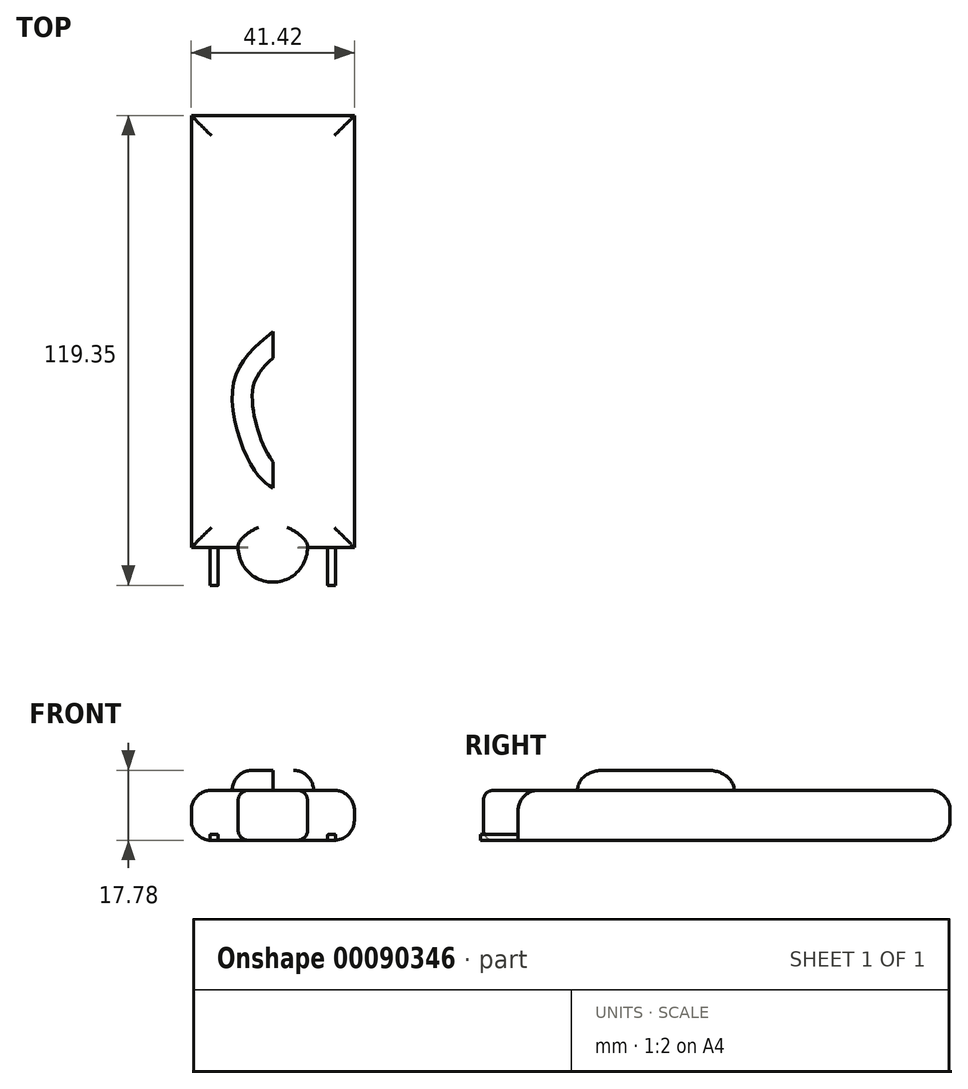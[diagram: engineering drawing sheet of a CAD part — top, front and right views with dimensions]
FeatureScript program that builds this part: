
annotation { "Feature Type Name" : "Feature", "Feature Type Description" : "" }
export const myFeature = defineFeature(function(context is Context, id is Id, definition is map)
    precondition{}
    {
        {
            var Q0;
            Q0=qCreatedBy(makeId("Top.planeOp"),FACE);
            var sketch = newSketch(context, id + "F0", { "sketchPlane" : qUnion([Q0])});
            skLineSegment(sketch, "E0.bottom", {"start": v(20.7, 54.87) * mm, "end": v(-20.7, 54.87) * mm});
            skLineSegment(sketch, "E0.top", {"start": v(20.7, -54.87) * mm, "end": v(-20.7, -54.87) * mm});
            skLineSegment(sketch, "E0.left", {"start": v(20.7, 54.87) * mm, "end": v(20.7, -54.87) * mm});
            skLineSegment(sketch, "E0.right", {"start": v(-20.7, 54.87) * mm, "end": v(-20.7, -54.87) * mm});
            skPoint(sketch, "E0.middle", {"position": v(0, 0) * mm});
            skLineSegment(sketch, "E1.bottom", {"start": v(15.97, -64.48) * mm, "end": v(13.9, -64.48) * mm});
            skLineSegment(sketch, "E1.top", {"start": v(15.97, -45.26) * mm, "end": v(13.9, -45.26) * mm});
            skLineSegment(sketch, "E1.left", {"start": v(15.97, -64.48) * mm, "end": v(15.97, -45.26) * mm});
            skLineSegment(sketch, "E1.right", {"start": v(13.9, -64.48) * mm, "end": v(13.9, -45.26) * mm});
            skPoint(sketch, "E1.middle", {"position": v(14.94, -54.87) * mm});
            skCircle(sketch, "E2", {"center": v(0, -54.87) * mm, "radius": 8.8 * mm});
            skLineSegment(sketch, "E3", {"start": v(0, 62.86) * mm, "end": v(0, -73.65) * mm});
            skLineSegment(sketch, "E4.MirrorCS", {"start": v(-15.97, -64.48) * mm, "end": v(-15.97, -45.26) * mm});
            skLineSegment(sketch, "E5.MirrorCS", {"start": v(-13.9, -64.48) * mm, "end": v(-13.9, -45.26) * mm});
            skLineSegment(sketch, "E6.MirrorCS", {"start": v(-15.97, -64.48) * mm, "end": v(-13.9, -64.48) * mm});
            skLineSegment(sketch, "E7.MirrorCS", {"start": v(-15.97, -45.26) * mm, "end": v(-13.9, -45.26) * mm});
            skFitSpline(sketch, "E8", {"points": [v(0, 0) * mm, v(10.06, -13.46) * mm, v(5.03, -34.76) * mm, v(0, -39.78) * mm], "startDerivative": vector(37.63, -31.39) * mm, "endDerivative": vector(-21.28, -14.76) * mm});
            skFitSpline(sketch, "E9.MirrorCS", {"points": [v(0, 0) * mm, v(-10.06, -13.46) * mm, v(-5.03, -34.76) * mm, v(0, -39.78) * mm], "startDerivative": vector(-37.63, -31.39) * mm, "endDerivative": vector(21.28, -14.76) * mm});
            skCircle(sketch, "E10", {"center": v(0, 15.96) * mm, "radius": 11.4 * mm});
            skSolve(sketch);
        }
        {
            var Q0;
            {var subQ12=sQuery(id+"F0.wireOp",EDGE,"E0.right");Q0=makeQuery(id+"F0.imprint","IMPRINT",FACE,{"disambiguationData":[TD([[makeQuery(id+"F0.imprint","IMPRINT",EDGE,{"derivedFrom":subQ12}),1.0]])]});}
            var Q1;
            {var subQ14=sQuery(id+"F0.wireOp",EDGE,"E0.left");Q1=makeQuery(id+"F0.imprint","IMPRINT",FACE,{"disambiguationData":[TD([[makeQuery(id+"F0.imprint","IMPRINT",EDGE,{"derivedFrom":subQ14}),-1.0]])]});}
            var Q2;
            {var subQ5=sQuery(id+"F0.wireOp",EDGE,"E1.top");Q2=makeQuery(id+"F0.imprint","IMPRINT",FACE,{"disambiguationData":[TD([[makeQuery(id+"F0.imprint","IMPRINT",EDGE,{"derivedFrom":subQ5}),1.0]])]});}
            var Q3;
            {var subQ5=sQuery(id+"F0.wireOp",EDGE,"E7.MirrorCS");Q3=makeQuery(id+"F0.imprint","IMPRINT",FACE,{"disambiguationData":[TD([[makeQuery(id+"F0.imprint","IMPRINT",EDGE,{"derivedFrom":subQ5}),-1.0]])]});}
            var Q4;
            {var subQ0=sQuery(id+"F0.wireOp",EDGE,"E2");var subQ1=sQuery(id+"F0.wireOp",EDGE,"E0.top");var subQ2=makeQuery(id+"F0.imprint","INTERSECT",VERTEX,{"disambiguationData":[OD(1.0)],"derivedFrom":[subQ1,subQ0]});Q4=makeQuery(id+"F0.imprint","IMPRINT",FACE,{"disambiguationData":[TD([[makeQuery(id+"F0.imprint","IMPRINT",EDGE,{"disambiguationData":[TD([[subQ2,1.0]])],"derivedFrom":subQ1}),-1.0]])]});}
            var Q5;
            {var subQ0=sQuery(id+"F0.wireOp",EDGE,"E2");var subQ1=sQuery(id+"F0.wireOp",EDGE,"E0.top");var subQ2=makeQuery(id+"F0.imprint","INTERSECT",VERTEX,{"disambiguationData":[OD(0.0)],"derivedFrom":[subQ1,subQ0]});Q5=makeQuery(id+"F0.imprint","IMPRINT",FACE,{"disambiguationData":[TD([[makeQuery(id+"F0.imprint","IMPRINT",EDGE,{"disambiguationData":[TD([[subQ2,-1.0]])],"derivedFrom":subQ1}),-1.0]])]});}
            extrude(context, id + "F1", {"entities" : qUnion([Q0, Q1, Q2, Q3, Q4, Q5]), "depth" : 12.7 * mm});
        }
        {
            var Q0;
            {var subQ0=sQuery(id+"F0.wireOp",EDGE,"E9.MirrorCS");Q0=makeQuery(id+"F0.imprint","IMPRINT",FACE,{"disambiguationData":[TD([[makeQuery(id+"F0.imprint","IMPRINT",EDGE,{"derivedFrom":subQ0}),1.0]])]});}
            var Q1;
            {var subQ1=sQuery(id+"F0.wireOp",EDGE,"E8");Q1=makeQuery(id+"F0.imprint","IMPRINT",FACE,{"disambiguationData":[TD([[makeQuery(id+"F0.imprint","IMPRINT",EDGE,{"derivedFrom":subQ1}),-1.0]])]});}
            extrude(context, id + "F2", {"entities" : qUnion([Q0, Q1]), "operationType" : NewBodyOperationType.ADD, "depth" : 17.78 * mm});
        }
        {
            var Q0;
            {var subQ0=sQuery(id+"F0.wireOp",EDGE,"E2");var subQ1=sQuery(id+"F0.wireOp",EDGE,"E0.top");var subQ2=makeQuery(id+"F0.imprint","INTERSECT",VERTEX,{"disambiguationData":[OD(1.0)],"derivedFrom":[subQ1,subQ0]});Q0=makeQuery(id+"F0.imprint","IMPRINT",FACE,{"disambiguationData":[TD([[makeQuery(id+"F0.imprint","IMPRINT",EDGE,{"disambiguationData":[TD([[subQ2,1.0]])],"derivedFrom":subQ1}),1.0]])]});}
            var Q1;
            {var subQ0=sQuery(id+"F0.wireOp",EDGE,"E2");var subQ1=sQuery(id+"F0.wireOp",EDGE,"E0.top");var subQ2=makeQuery(id+"F0.imprint","INTERSECT",VERTEX,{"disambiguationData":[OD(0.0)],"derivedFrom":[subQ1,subQ0]});Q1=makeQuery(id+"F0.imprint","IMPRINT",FACE,{"disambiguationData":[TD([[makeQuery(id+"F0.imprint","IMPRINT",EDGE,{"disambiguationData":[TD([[subQ2,-1.0]])],"derivedFrom":subQ1}),1.0]])]});}
            extrude(context, id + "F3", {"entities" : qUnion([Q0, Q1]), "operationType" : NewBodyOperationType.ADD, "depth" : 12.7 * mm});
        }
        {
            var Q0;
            {var subQ5=sQuery(id+"F0.wireOp",EDGE,"E1.bottom");Q0=makeQuery(id+"F0.imprint","IMPRINT",FACE,{"disambiguationData":[TD([[makeQuery(id+"F0.imprint","IMPRINT",EDGE,{"derivedFrom":subQ5}),-1.0]])]});}
            var Q1;
            {var subQ5=sQuery(id+"F0.wireOp",EDGE,"E6.MirrorCS");Q1=makeQuery(id+"F0.imprint","IMPRINT",FACE,{"disambiguationData":[TD([[makeQuery(id+"F0.imprint","IMPRINT",EDGE,{"derivedFrom":subQ5}),1.0]])]});}
            extrude(context, id + "F4", {"entities" : qUnion([Q0, Q1]), "operationType" : NewBodyOperationType.ADD, "depth" : 1.52 * mm});
        }
        {
            var Q0;
            Q0=makeQuery(id+"F1.opExtrude","CAP_EDGE",EDGE,{"disambiguationData":[OSD([sQuery(id+"F0.wireOp",EDGE,"E0.right")])],"isStart":false});
            var Q1;
            Q1=makeQuery(id+"F1.opExtrude","CAP_EDGE",EDGE,{"disambiguationData":[OSD([sQuery(id+"F0.wireOp",EDGE,"E0.right")])],"isStart":true});
            var Q2;
            Q2=makeQuery(id+"F1.opExtrude","CAP_EDGE",EDGE,{"disambiguationData":[OSD([sQuery(id+"F0.wireOp",EDGE,"E0.bottom")])],"isStart":false});
            var Q3;
            Q3=makeQuery(id+"F1.opExtrude","CAP_EDGE",EDGE,{"disambiguationData":[OSD([sQuery(id+"F0.wireOp",EDGE,"E0.bottom")])],"isStart":true});
            var Q4;
            Q4=makeQuery(id+"F1.opExtrude","CAP_EDGE",EDGE,{"disambiguationData":[OSD([sQuery(id+"F0.wireOp",EDGE,"E0.left")])],"isStart":false});
            var Q5;
            {var subQ1=sQuery(id+"F0.wireOp",EDGE,"E0.top");var subQ2=sQuery(id+"F0.wireOp",EDGE,"E0.left");Q5=makeQuery(id+"F3.boolean.opBoolean","SPLIT",EDGE,{"disambiguationData":[TD([makeQuery(id+"F1.opExtrude","SWEPT_FACE",FACE,{"disambiguationData":[OSD([subQ2])]})])],"derivedFrom":makeQuery(id+"F1.opExtrude","CAP_EDGE",EDGE,{"disambiguationData":[OSD([subQ1])],"isStart":false})});}
            var Q6;
            Q6=makeQuery(id+"F1.opExtrude","CAP_EDGE",EDGE,{"disambiguationData":[OSD([sQuery(id+"F0.wireOp",EDGE,"E0.left")])],"isStart":true});
            var Q7;
            {var subQ1=sQuery(id+"F0.wireOp",EDGE,"E0.top");var subQ2=sQuery(id+"F0.wireOp",EDGE,"E0.right");Q7=makeQuery(id+"F3.boolean.opBoolean","SPLIT",EDGE,{"disambiguationData":[TD([makeQuery(id+"F1.opExtrude","SWEPT_FACE",FACE,{"disambiguationData":[OSD([subQ2])]})])],"derivedFrom":makeQuery(id+"F1.opExtrude","CAP_EDGE",EDGE,{"disambiguationData":[OSD([subQ1])],"isStart":false})});}
            fillet(context, id + "F5", {"entities" : qUnion([Q0, Q1, Q2, Q3, Q4, Q5, Q6, Q7]), "radius" : 5.08 * mm, "tangentPropagation" : true, "allowEdgeOverflow" : false});
        }
        {
            var Q0;
            Q0=makeQuery(id+"F3.opExtrude","CAP_EDGE",EDGE,{"disambiguationData":[OSD([sQuery(id+"F0.wireOp",EDGE,"E2")])],"isStart":false});
            var Q1;
            Q1=makeQuery(id+"F3.opExtrude","CAP_EDGE",EDGE,{"disambiguationData":[OSD([sQuery(id+"F0.wireOp",EDGE,"E2")])],"isStart":true});
            fillet(context, id + "F6", {"entities" : qUnion([Q0, Q1]), "radius" : 2.54 * mm, "tangentPropagation" : true, "allowEdgeOverflow" : false});
        }
        {
            var Q0;
            Q0=makeQuery(id+"F2.opExtrude","CAP_EDGE",EDGE,{"disambiguationData":[OSD([sQuery(id+"F0.wireOp",EDGE,"E9.MirrorCS")])],"isStart":false});
            var Q1;
            Q1=makeQuery(id+"F2.opExtrude","CAP_EDGE",EDGE,{"disambiguationData":[OSD([sQuery(id+"F0.wireOp",EDGE,"E8")])],"isStart":false});
            fillet(context, id + "F7", {"entities" : qUnion([Q0, Q1]), "radius" : 5.08 * mm, "tangentPropagation" : true, "allowEdgeOverflow" : false});
        }
        {
            var Q0;
            Q0=makeQuery(id+"F4.opExtrude","CAP_EDGE",EDGE,{"disambiguationData":[OSD([sQuery(id+"F0.wireOp",EDGE,"E1.left")])],"isStart":false});
            var Q1;
            {var subQ0=sQuery(id+"F0.wireOp",EDGE,"E0.top");var subQ1=sQuery(id+"F0.wireOp",EDGE,"E9.MirrorCS");var subQ2=sQuery(id+"F0.wireOp",EDGE,"E8");var subQ3=sQuery(id+"F0.wireOp",EDGE,"E0.left");Q1=makeQuery(id+"F5.opFillet","BLEND_EDGE",EDGE,{"blendedFrom":[makeQuery(id+"F1.opExtrude","CAP_EDGE",EDGE,{"disambiguationData":[OSD([subQ3])],"isStart":true}),makeQuery(id+"F4.boolean.opBoolean","MERGE",FACE,{"derivedFrom":[makeQuery(id+"F3.boolean.opBoolean","MERGE",FACE,{"derivedFrom":[makeQuery(id+"F2.boolean.opBoolean","MERGE",FACE,{"derivedFrom":[makeQuery(id+"F1.opExtrude","CAP_FACE",FACE,{"disambiguationData":[OSD([sQuery(id+"F0.wireOp",EDGE,"E0.bottom"),subQ0,subQ3,sQuery(id+"F0.wireOp",EDGE,"E0.right"),subQ2,subQ1])],"isStart":true}),makeQuery(id+"F2.opExtrude","CAP_FACE",FACE,{"disambiguationData":[OSD([subQ2,subQ1])],"isStart":true})]}),makeQuery(id+"F3.opExtrude","CAP_FACE",FACE,{"disambiguationData":[OSD([subQ0,sQuery(id+"F0.wireOp",EDGE,"E2")])],"isStart":true})]}),makeQuery(id+"F4.opExtrude","CAP_FACE",FACE,{"disambiguationData":[OSD([subQ0,sQuery(id+"F0.wireOp",EDGE,"E1.bottom"),sQuery(id+"F0.wireOp",EDGE,"E1.left"),sQuery(id+"F0.wireOp",EDGE,"E1.right")])],"isStart":true}),makeQuery(id+"F4.opExtrude","CAP_FACE",FACE,{"disambiguationData":[OSD([subQ0,sQuery(id+"F0.wireOp",EDGE,"E4.MirrorCS"),sQuery(id+"F0.wireOp",EDGE,"E5.MirrorCS"),sQuery(id+"F0.wireOp",EDGE,"E6.MirrorCS")])],"isStart":true})]})],"blendedInto":[makeQuery(id+"F4.boolean.opBoolean","MERGE",FACE,{"derivedFrom":[makeQuery(id+"F3.boolean.opBoolean","MERGE",FACE,{"derivedFrom":[makeQuery(id+"F2.boolean.opBoolean","MERGE",FACE,{"derivedFrom":[makeQuery(id+"F1.opExtrude","CAP_FACE",FACE,{"disambiguationData":[OSD([sQuery(id+"F0.wireOp",EDGE,"E0.bottom"),subQ0,subQ3,sQuery(id+"F0.wireOp",EDGE,"E0.right"),subQ2,subQ1])],"isStart":true}),makeQuery(id+"F2.opExtrude","CAP_FACE",FACE,{"disambiguationData":[OSD([subQ2,subQ1])],"isStart":true})]}),makeQuery(id+"F3.opExtrude","CAP_FACE",FACE,{"disambiguationData":[OSD([subQ0,sQuery(id+"F0.wireOp",EDGE,"E2")])],"isStart":true})]}),makeQuery(id+"F4.opExtrude","CAP_FACE",FACE,{"disambiguationData":[OSD([subQ0,sQuery(id+"F0.wireOp",EDGE,"E1.bottom"),sQuery(id+"F0.wireOp",EDGE,"E1.left"),sQuery(id+"F0.wireOp",EDGE,"E1.right")])],"isStart":true}),makeQuery(id+"F4.opExtrude","CAP_FACE",FACE,{"disambiguationData":[OSD([subQ0,sQuery(id+"F0.wireOp",EDGE,"E4.MirrorCS"),sQuery(id+"F0.wireOp",EDGE,"E5.MirrorCS"),sQuery(id+"F0.wireOp",EDGE,"E6.MirrorCS")])],"isStart":true})]})]});}
            var Q2;
            Q2=makeQuery(id+"F4.opExtrude","CAP_EDGE",EDGE,{"disambiguationData":[OSD([sQuery(id+"F0.wireOp",EDGE,"E1.right")])],"isStart":false});
            var Q3;
            Q3=makeQuery(id+"F4.opExtrude","CAP_EDGE",EDGE,{"disambiguationData":[OSD([sQuery(id+"F0.wireOp",EDGE,"E1.right")])],"isStart":true});
            var Q4;
            Q4=makeQuery(id+"F4.opExtrude","CAP_EDGE",EDGE,{"disambiguationData":[OSD([sQuery(id+"F0.wireOp",EDGE,"E4.MirrorCS")])],"isStart":false});
            var Q5;
            Q5=makeQuery(id+"F5.opFillet","BLEND_EDGE",EDGE,{"blendedFrom":[makeQuery(id+"F1.opExtrude","CAP_EDGE",EDGE,{"disambiguationData":[OSD([sQuery(id+"F0.wireOp",EDGE,"E0.right")])],"isStart":true}),makeQuery(id+"F4.opExtrude","SWEPT_FACE",FACE,{"disambiguationData":[OSD([sQuery(id+"F0.wireOp",EDGE,"E4.MirrorCS")])]})],"blendedInto":[makeQuery(id+"F4.opExtrude","SWEPT_FACE",FACE,{"disambiguationData":[OSD([sQuery(id+"F0.wireOp",EDGE,"E4.MirrorCS")])]})]});
            var Q6;
            Q6=makeQuery(id+"F4.opExtrude","CAP_EDGE",EDGE,{"disambiguationData":[OSD([sQuery(id+"F0.wireOp",EDGE,"E5.MirrorCS")])],"isStart":false});
            var Q7;
            Q7=makeQuery(id+"F4.opExtrude","CAP_EDGE",EDGE,{"disambiguationData":[OSD([sQuery(id+"F0.wireOp",EDGE,"E5.MirrorCS")])],"isStart":true});
            fillet(context, id + "F8", {"entities" : qUnion([Q0, Q1, Q2, Q3, Q4, Q5, Q6, Q7]), "radius" : 0.25 * mm, "tangentPropagation" : true, "allowEdgeOverflow" : false});
        }
        {
            var Q0;
            {var subQ0=sQuery(id+"F0.wireOp",EDGE,"E10");var subQ1=sQuery(id+"F0.wireOp",EDGE,"E3");var subQ2=makeQuery(id+"F0.imprint","INTERSECT",VERTEX,{"disambiguationData":[OD(0.0)],"derivedFrom":[subQ1,subQ0]});Q0=makeQuery(id+"F0.imprint","IMPRINT",FACE,{"disambiguationData":[TD([[makeQuery(id+"F0.imprint","IMPRINT",EDGE,{"disambiguationData":[TD([[subQ2,-1.0]])],"derivedFrom":subQ1}),1.0]])]});}
            var Q1;
            {var subQ0=sQuery(id+"F0.wireOp",EDGE,"E10");var subQ1=sQuery(id+"F0.wireOp",EDGE,"E3");var subQ2=makeQuery(id+"F0.imprint","INTERSECT",VERTEX,{"disambiguationData":[OD(0.0)],"derivedFrom":[subQ1,subQ0]});Q1=makeQuery(id+"F0.imprint","IMPRINT",FACE,{"disambiguationData":[TD([[makeQuery(id+"F0.imprint","IMPRINT",EDGE,{"disambiguationData":[TD([[subQ2,-1.0]])],"derivedFrom":subQ1}),-1.0]])]});}
            extrude(context, id + "F9", {"entities" : qUnion([Q0, Q1]), "operationType" : NewBodyOperationType.ADD, "depth" : 12.7 * mm});
        }
    });
